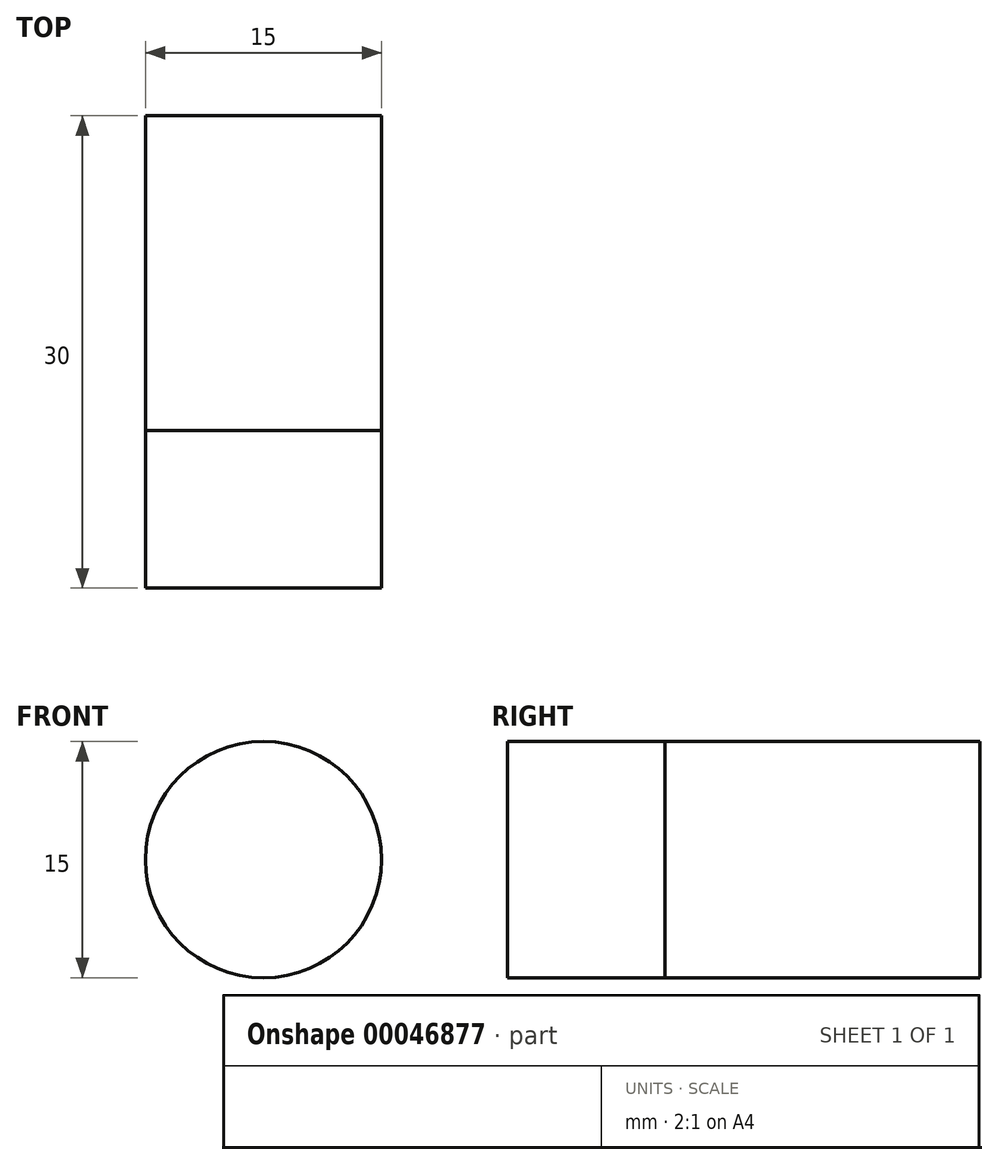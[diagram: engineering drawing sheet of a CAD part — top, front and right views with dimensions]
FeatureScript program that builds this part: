
annotation { "Feature Type Name" : "Feature", "Feature Type Description" : "" }
export const myFeature = defineFeature(function(context is Context, id is Id, definition is map)
    precondition{}
    {
        {
            var Q0;
            Q0=qCreatedBy(makeId("Front.planeOp"),FACE);
            var sketch = newSketch(context, id + "F0", { "sketchPlane" : qUnion([Q0])});
            skCircle(sketch, "E0", {"center": v(0, 0) * mm, "radius": 7.5 * mm});
            skSolve(sketch);
        }
        {
            var Q0;
            Q0 = qSketchRegion(id + "F0", true);
            extrude(context, id + "F1", {"entities" : qUnion([Q0]), "depth" : 20 * mm});
        }
        {
            var Q0;
            Q0 = qSketchRegion(id + "F0", true);
            extrude(context, id + "F2", {"entities" : qUnion([Q0]), "depth" : 30 * mm});
        }
    });
